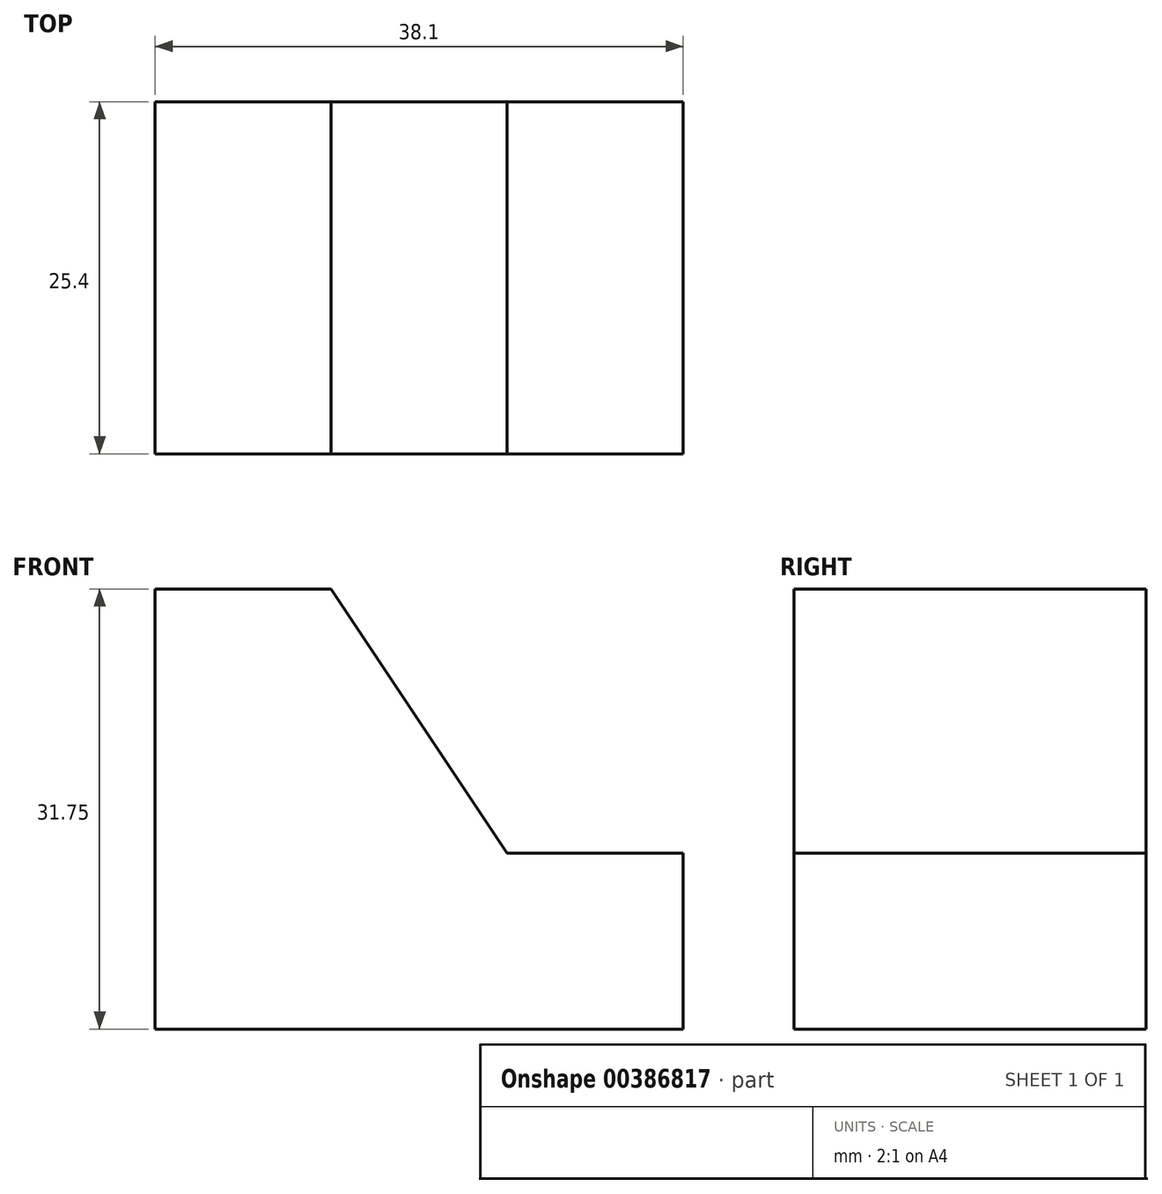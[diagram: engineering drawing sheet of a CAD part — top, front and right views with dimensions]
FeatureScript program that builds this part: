
annotation { "Feature Type Name" : "Feature", "Feature Type Description" : "" }
export const myFeature = defineFeature(function(context is Context, id is Id, definition is map)
    precondition{}
    {
        {
            var Q0;
            Q0=qCreatedBy(makeId("Top.planeOp"),FACE);
            var sketch = newSketch(context, id + "F0", { "sketchPlane" : qUnion([Q0])});
            skLineSegment(sketch, "E0", {"start": v(-21.07, -10.44) * mm, "end": v(17.03, -10.44) * mm});
            skLineSegment(sketch, "E1", {"start": v(-21.07, -10.44) * mm, "end": v(-21.07, 14.96) * mm});
            skLineSegment(sketch, "E2", {"start": v(-21.07, 14.96) * mm, "end": v(17.03, 14.96) * mm});
            skLineSegment(sketch, "E3", {"start": v(17.03, 14.96) * mm, "end": v(17.03, -10.44) * mm});
            skSolve(sketch);
        }
        {
            var Q0;
            Q0=makeQuery(id+"F0.imprint","IMPRINT",FACE,{"disambiguationData":[TD([[makeQuery(id+"F0.imprint","IMPRINT",EDGE,{"derivedFrom":sQuery(id+"F0.wireOp",EDGE,"E0")}),1.0]])]});
            extrude(context, id + "F1", {"entities" : qUnion([Q0]), "depth" : 12.7 * mm});
        }
        {
            var Q0;
            Q0=makeQuery(id+"F1.opExtrude","CAP_FACE",FACE,{"disambiguationData":[OSD([sQuery(id+"F0.wireOp",EDGE,"E0"),sQuery(id+"F0.wireOp",EDGE,"E1"),sQuery(id+"F0.wireOp",EDGE,"E2"),sQuery(id+"F0.wireOp",EDGE,"E3")])],"isStart":false});
            var sketch = newSketch(context, id + "F2", { "sketchPlane" : qUnion([Q0])});
            skLineSegment(sketch, "E4", {"start": v(-21.07, 14.96) * mm, "end": v(4.33, 14.96) * mm});
            skLineSegment(sketch, "E5", {"start": v(4.33, 14.96) * mm, "end": v(4.33, -10.44) * mm});
            skLineSegment(sketch, "E6", {"start": v(4.33, -10.44) * mm, "end": v(-21.07, -10.44) * mm});
            skLineSegment(sketch, "E7", {"start": v(-21.07, -10.44) * mm, "end": v(-21.07, 14.96) * mm});
            skSolve(sketch);
        }
        {
            var Q0;
            Q0=makeQuery(id+"F2.imprint","IMPRINT",FACE,{"disambiguationData":[TD([[makeQuery(id+"F2.imprint","IMPRINT",EDGE,{"derivedFrom":sQuery(id+"F2.wireOp",EDGE,"E4")}),-1.0]])]});
            var sketch = newSketch(context, id + "F3", { "sketchPlane" : qUnion([Q0])});
            skLineSegment(sketch, "E8", {"start": v(-21.26, 15.3) * mm, "end": v(-8.56, 15.3) * mm});
            skLineSegment(sketch, "E9", {"start": v(-8.56, 15.3) * mm, "end": v(-8.56, -10.1) * mm});
            skLineSegment(sketch, "E10", {"start": v(-8.56, -10.1) * mm, "end": v(-21.26, -10.1) * mm});
            skLineSegment(sketch, "E11", {"start": v(-21.26, -10.1) * mm, "end": v(-21.26, 15.3) * mm});
            skSolve(sketch);
        }
        {
            var Q0;
            {var subQ0=sQuery(id+"F3.wireOp",EDGE,"E10");var subQ1=sQuery(id+"F3.wireOp",EDGE,"E9");var subQ2=makeQuery(id+"F3.imprint","INTERSECT",VERTEX,{"derivedFrom":[subQ1,subQ0]});Q0=makeQuery(id+"F3.imprint","IMPRINT",FACE,{"disambiguationData":[TD([[makeQuery(id+"F3.imprint","IMPRINT",EDGE,{"disambiguationData":[TD([[subQ2,1.0]])],"derivedFrom":subQ1}),-1.0]])]});}
            extrude(context, id + "F4", {"entities" : qUnion([Q0]), "operationType" : NewBodyOperationType.ADD, "depth" : 19.05 * mm});
        }
        {
            var Q0;
            Q0=makeQuery(id+"F2.imprint","IMPRINT",FACE,{"disambiguationData":[TD([[makeQuery(id+"F2.imprint","IMPRINT",EDGE,{"derivedFrom":sQuery(id+"F2.wireOp",EDGE,"E4")}),-1.0]])]});
            extrude(context, id + "F5", {"entities" : qUnion([Q0]), "operationType" : NewBodyOperationType.ADD, "depth" : 19.05 * mm});
        }
        {
            var Q0;
            Q0=makeQuery(id+"F5.boolean.opBoolean","MERGE",FACE,{"derivedFrom":[makeQuery(id+"F1.opExtrude","SWEPT_FACE",FACE,{"disambiguationData":[OSD([sQuery(id+"F0.wireOp",EDGE,"E0")])]}),makeQuery(id+"F5.opExtrude","SWEPT_FACE",FACE,{"disambiguationData":[OSD([sQuery(id+"F2.wireOp",EDGE,"E6")])]})]});
            var sketch = newSketch(context, id + "F6", { "sketchPlane" : qUnion([Q0])});
            skLineSegment(sketch, "E12", {"start": v(-21.07, 31.75) * mm, "end": v(-8.37, 31.75) * mm});
            skLineSegment(sketch, "E13", {"start": v(4.33, 12.7) * mm, "end": v(-8.37, 31.75) * mm});
            skSolve(sketch);
        }
        {
            var Q0;
            {var subQ0=sQuery(id+"F6.wireOp",EDGE,"E13");Q0=makeQuery(id+"F6.imprint","IMPRINT",FACE,{"disambiguationData":[TD([[makeQuery(id+"F6.imprint","IMPRINT",EDGE,{"derivedFrom":subQ0}),-1.0]])]});}
            var sketch = newSketch(context, id + "F7", { "sketchPlane" : qUnion([Q0])});
            skSolve(sketch);
        }
        {
            var Q0;
            {var subQ0=sQuery(id+"F6.wireOp",EDGE,"E13");Q0=makeQuery(id+"F6.imprint","IMPRINT",FACE,{"disambiguationData":[TD([[makeQuery(id+"F6.imprint","IMPRINT",EDGE,{"derivedFrom":subQ0}),-1.0]])]});}
            extrude(context, id + "F8", {"entities" : qUnion([Q0]), "operationType" : NewBodyOperationType.ADD, "depth" : -25.4 * mm});
        }
        {
            var Q0;
            {var subQ0=sQuery(id+"F6.wireOp",EDGE,"E13");Q0=makeQuery(id+"F7.imprint","IMPRINT",FACE,{"disambiguationData":[TD([[makeQuery(id+"F7.imprint","IMPRINT",EDGE,{"derivedFrom":makeQuery(id+"F6.imprint","IMPRINT",EDGE,{"derivedFrom":subQ0})}),-1.0]])]});}
            extrude(context, id + "F9", {"entities" : qUnion([Q0]), "operationType" : NewBodyOperationType.REMOVE, "oppositeDirection" : true, "depth" : 25.4 * mm});
        }
    });
